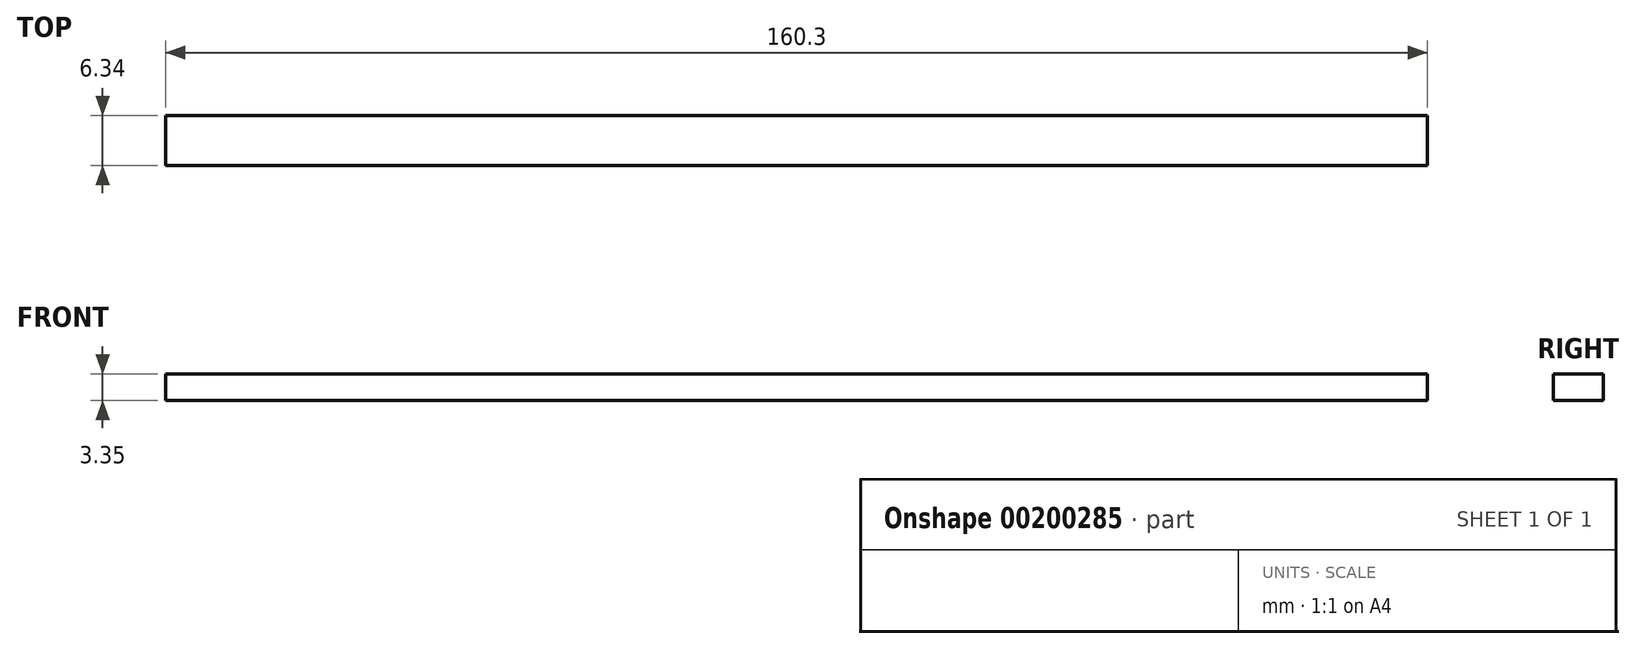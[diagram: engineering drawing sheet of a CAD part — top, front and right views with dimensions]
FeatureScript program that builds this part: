
annotation { "Feature Type Name" : "Feature", "Feature Type Description" : "" }
export const myFeature = defineFeature(function(context is Context, id is Id, definition is map)
    precondition{}
    {
        {
            var Q0;
            Q0=qCreatedBy(makeId("Top.planeOp"),FACE);
            var sketch = newSketch(context, id + "F0", { "sketchPlane" : qUnion([Q0])});
            skLineSegment(sketch, "E0.bottom", {"start": v(80.15, -3.17) * mm, "end": v(-80.15, -3.17) * mm});
            skLineSegment(sketch, "E0.top", {"start": v(80.15, 3.18) * mm, "end": v(-80.15, 3.17) * mm});
            skLineSegment(sketch, "E0.left", {"start": v(80.15, -3.17) * mm, "end": v(80.15, 3.18) * mm});
            skLineSegment(sketch, "E0.right", {"start": v(-80.15, -3.17) * mm, "end": v(-80.15, 3.18) * mm});
            skPoint(sketch, "E0.middle", {"position": v(0, 0) * mm});
            skSolve(sketch);
        }
        {
            var Q0;
            Q0 = qSketchRegion(id + "F0", true);
            extrude(context, id + "F1", {"entities" : qUnion([Q0]), "depth" : 3.35 * mm, "offsetDistance" : 25 * mm});
        }
    });
